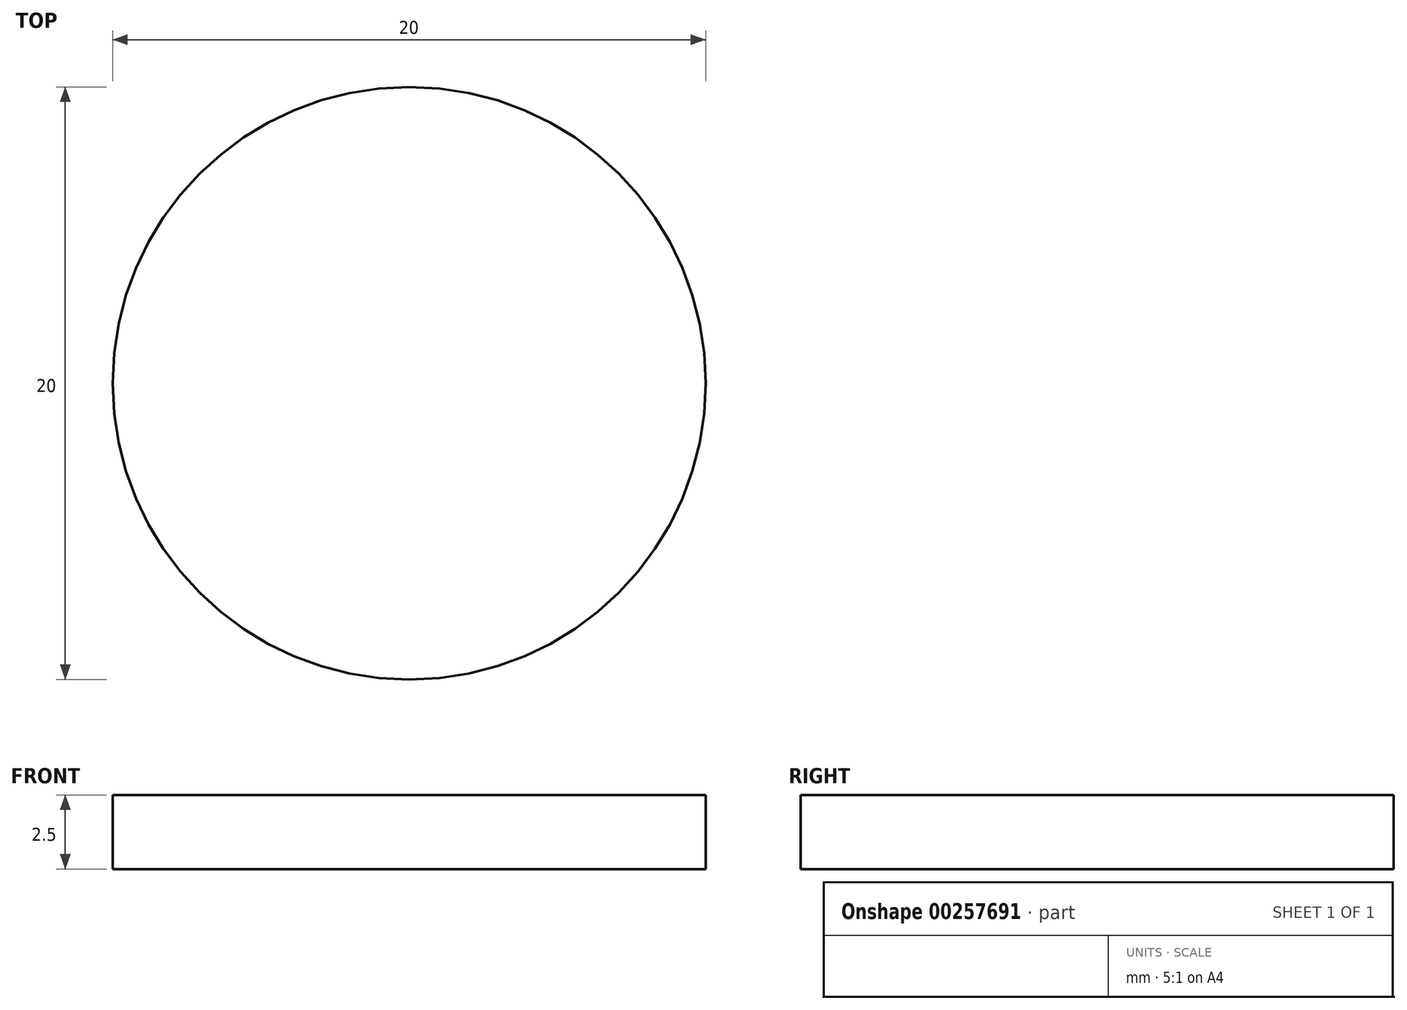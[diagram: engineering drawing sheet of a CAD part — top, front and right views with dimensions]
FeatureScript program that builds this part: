
annotation { "Feature Type Name" : "Feature", "Feature Type Description" : "" }
export const myFeature = defineFeature(function(context is Context, id is Id, definition is map)
    precondition{}
    {
        {
            var Q0;
            Q0=qCreatedBy(makeId("Top.planeOp"),FACE);
            var sketch = newSketch(context, id + "F0", { "sketchPlane" : qUnion([Q0])});
            skCircle(sketch, "E0", {"center": v(0, 0) * mm, "radius": 10 * mm});
            skSolve(sketch);
        }
        {
            var Q0;
            Q0=makeQuery(id+"F0.imprint","IMPRINT",FACE,{"disambiguationData":[TD([[makeQuery(id+"F0.imprint","IMPRINT",EDGE,{"derivedFrom":sQuery(id+"F0.wireOp",EDGE,"E0")}),1.0]])]});
            var Q1;
            Q1=sQuery(id+"F0.wireOp",EDGE,"E0");
            extrude(context, id + "F1", {"entities" : qUnion([Q0]), "surfaceEntities" : qUnion([Q1]), "depth" : 50 * mm});
        }
        {
            var Q0;
            Q0=makeQuery(id+"F1.opExtrude","CAP_FACE",FACE,{"disambiguationData":[OSD([sQuery(id+"F0.wireOp",EDGE,"E0")])],"isStart":false});
            var Q1;
            Q1=makeQuery(id+"F1.opExtrude","SWEPT_FACE",FACE,{"disambiguationData":[OSD([sQuery(id+"F0.wireOp",EDGE,"E0")])]});
            shell(context, id + "F2", {"entities" : qUnion([Q0, Q1]), "thickness" : 2.5 * mm});
        }
    });
